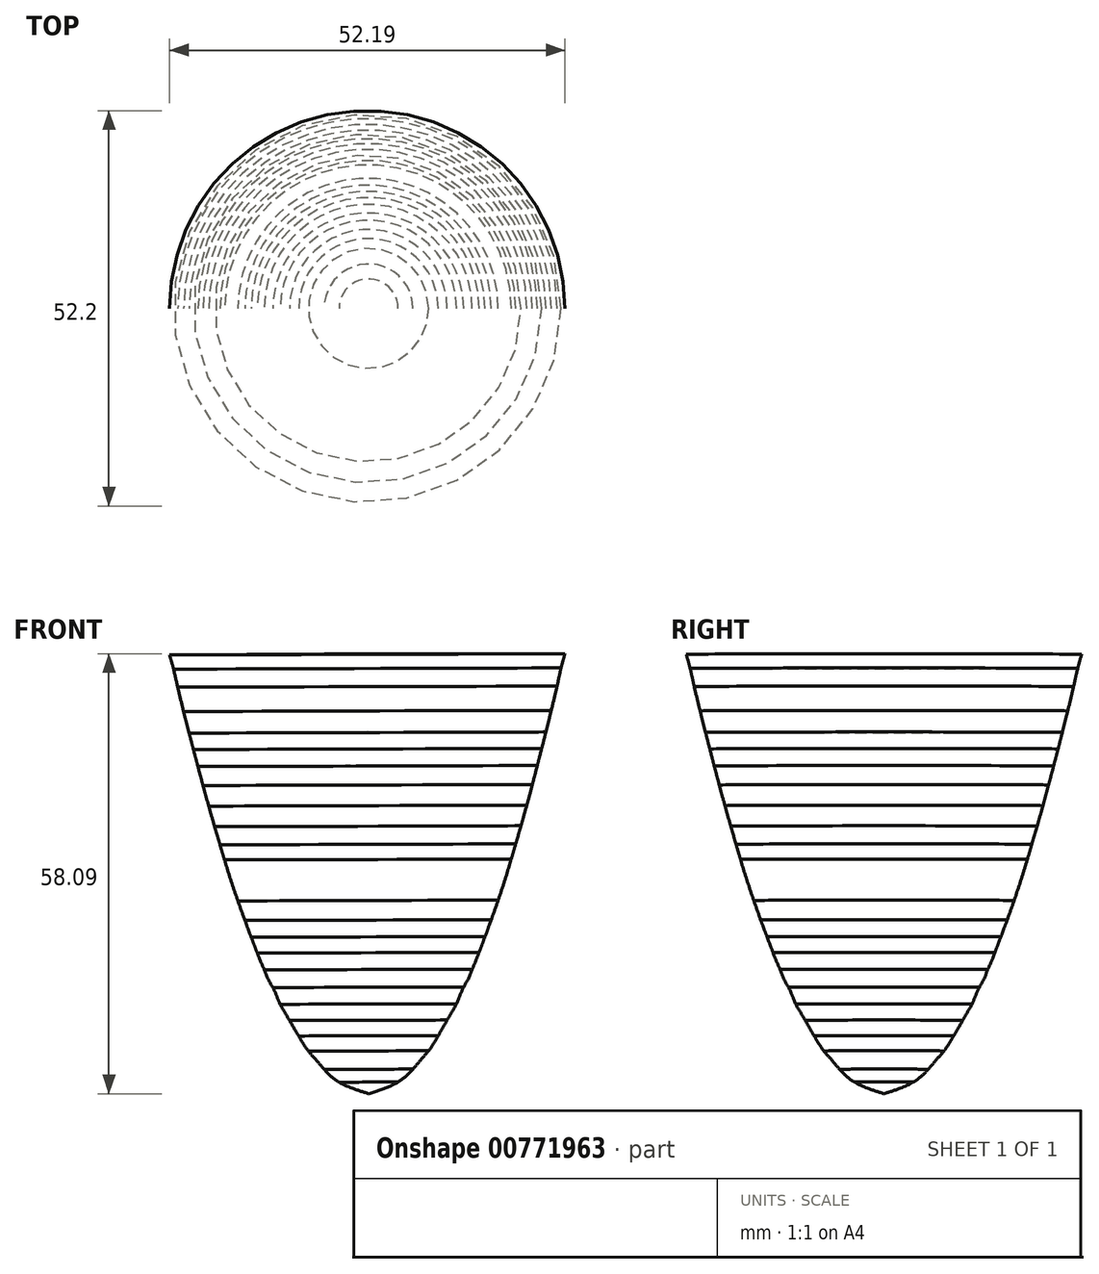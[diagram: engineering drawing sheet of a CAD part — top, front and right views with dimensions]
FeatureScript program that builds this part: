
annotation { "Feature Type Name" : "Feature", "Feature Type Description" : "" }
export const myFeature = defineFeature(function(context is Context, id is Id, definition is map)
    precondition{}
    {
        {
            var Q0;
            Q0=qCreatedBy(makeId("Front.planeOp"),FACE);
            var sketch = newSketch(context, id + "F0", { "sketchPlane" : qUnion([Q0])});
            skPoint(sketch, "E0", {"position": v(0.03, -0.02) * mm});
            skPoint(sketch, "E1", {"position": v(3.18, 1.13) * mm});
            skPoint(sketch, "E2", {"position": v(5.18, 2.5) * mm});
            skPoint(sketch, "E3", {"position": v(6.84, 4.37) * mm});
            skPoint(sketch, "E4", {"position": v(8.16, 5.94) * mm});
            skPoint(sketch, "E5", {"position": v(9.14, 7.52) * mm});
            skPoint(sketch, "E6", {"position": v(9.9, 8.84) * mm});
            skPoint(sketch, "E7", {"position": v(10.89, 10.54) * mm});
            skPoint(sketch, "E8", {"position": v(11.75, 12.1) * mm});
            skPoint(sketch, "E9", {"position": v(12.46, 13.83) * mm});
            skPoint(sketch, "E10", {"position": v(13.16, 15.1) * mm});
            skPoint(sketch, "E11", {"position": v(13.63, 16.27) * mm});
            skPoint(sketch, "E12", {"position": v(14.18, 17.52) * mm});
            skPoint(sketch, "E13", {"position": v(14.76, 19.04) * mm});
            skPoint(sketch, "E14", {"position": v(15.34, 20.55) * mm});
            skPoint(sketch, "E15", {"position": v(15.91, 22.07) * mm});
            skPoint(sketch, "E16", {"position": v(16.5, 23.66) * mm});
            skPoint(sketch, "E17", {"position": v(17, 25.39) * mm});
            skPoint(sketch, "E18", {"position": v(17.57, 26.83) * mm});
            skPoint(sketch, "E19", {"position": v(18.15, 28.78) * mm});
            skPoint(sketch, "E20", {"position": v(18.73, 30.87) * mm});
            skPoint(sketch, "E21", {"position": v(19.45, 32.97) * mm});
            skPoint(sketch, "E22", {"position": v(20.25, 35.58) * mm});
            skPoint(sketch, "E23", {"position": v(20.68, 37.74) * mm});
            skPoint(sketch, "E24", {"position": v(21.38, 39.85) * mm});
            skPoint(sketch, "E25", {"position": v(22, 42.1) * mm});
            skPoint(sketch, "E26", {"position": v(22.47, 44.2) * mm});
            skPoint(sketch, "E27", {"position": v(23.18, 47) * mm});
            skPoint(sketch, "E28", {"position": v(24.03, 50.12) * mm});
            skPoint(sketch, "E29", {"position": v(24.81, 53.4) * mm});
            skPoint(sketch, "E30", {"position": v(25.43, 56.2) * mm});
            skPoint(sketch, "E31", {"position": v(25.43, 58.07) * mm});
            skFitSpline(sketch, "E32", {"points": [v(0.03, -0.02) * mm, v(3.18, 1.13) * mm, v(5.18, 2.5) * mm, v(6.84, 4.37) * mm, v(8.16, 5.94) * mm, v(9.14, 7.52) * mm, v(9.9, 8.84) * mm, v(10.89, 10.54) * mm, v(11.75, 12.1) * mm, v(12.46, 13.83) * mm, v(13.16, 15.1) * mm, v(13.63, 16.27) * mm, v(14.18, 17.52) * mm, v(14.76, 19.04) * mm, v(15.34, 20.55) * mm, v(17.57, 26.83) * mm, v(19.45, 32.97) * mm, v(21.38, 39.85) * mm, v(24.81, 53.4) * mm, v(25.43, 56.2) * mm, v(25.95, 58.07) * mm], "startDerivative": vector(61.74, 19.66) * mm, "endDerivative": vector(13.33, 46) * mm});
            skLineSegment(sketch, "E33", {"start": v(25.95, 58.07) * mm, "end": v(-0.15, 58.07) * mm});
            skLineSegment(sketch, "E34", {"start": v(-0.15, 58.07) * mm, "end": v(0.03, -0.02) * mm});
            skLineSegment(sketch, "E35", {"start": v(19.45, 32.97) * mm, "end": v(-0.07, 32.97) * mm});
            skLineSegment(sketch, "E36", {"start": v(25.43, 56.2) * mm, "end": v(-0.14, 56.12) * mm});
            skLineSegment(sketch, "E37", {"start": v(23.97, 45.58) * mm, "end": v(-6.54, 45.48) * mm});
            skLineSegment(sketch, "E38", {"start": v(-4.68, 53.8) * mm, "end": v(34.04, 53.8) * mm});
            skLineSegment(sketch, "E39", {"start": v(-7.24, 50.6) * mm, "end": v(41.15, 50.6) * mm});
            skLineSegment(sketch, "E40", {"start": v(-7.24, 47.74) * mm, "end": v(38.8, 47.74) * mm});
            skLineSegment(sketch, "E41", {"start": v(-6.54, 43.31) * mm, "end": v(33.08, 43.31) * mm});
            skLineSegment(sketch, "E42", {"start": v(-6.61, 40.8) * mm, "end": v(35.36, 40.8) * mm});
            skLineSegment(sketch, "E43", {"start": v(-6.34, 38.08) * mm, "end": v(33.86, 38.08) * mm});
            skLineSegment(sketch, "E44", {"start": v(-4.24, 35.28) * mm, "end": v(35.36, 35.4) * mm});
            skLineSegment(sketch, "E45", {"start": v(-4.66, 30.97) * mm, "end": v(35.36, 30.97) * mm});
            skLineSegment(sketch, "E46", {"start": v(-4.61, 28.25) * mm, "end": v(32.86, 28.25) * mm});
            skLineSegment(sketch, "E47", {"start": v(-4.44, 25.54) * mm, "end": v(32.3, 25.54) * mm});
            skLineSegment(sketch, "E48", {"start": v(-4.61, 22.96) * mm, "end": v(29.5, 22.96) * mm});
            skLineSegment(sketch, "E49", {"start": v(-4.36, 20.74) * mm, "end": v(30.66, 20.74) * mm});
            skLineSegment(sketch, "E50", {"start": v(-4.32, 18.64) * mm, "end": v(26.14, 18.64) * mm});
            skLineSegment(sketch, "E51", {"start": v(-4.53, 16.42) * mm, "end": v(28.75, 16.42) * mm});
            skLineSegment(sketch, "E52", {"start": v(-4.37, 14.08) * mm, "end": v(25.46, 14.08) * mm});
            skLineSegment(sketch, "E53", {"start": v(-4.32, 11.86) * mm, "end": v(28.46, 11.86) * mm});
            skLineSegment(sketch, "E54", {"start": v(-4.25, 9.7) * mm, "end": v(25.28, 9.7) * mm});
            skLineSegment(sketch, "E55", {"start": v(-4.22, 7.66) * mm, "end": v(30.42, 7.66) * mm});
            skLineSegment(sketch, "E56", {"start": v(-4.18, 5.62) * mm, "end": v(24.54, 5.7) * mm});
            skLineSegment(sketch, "E57", {"start": v(-4.14, 3.23) * mm, "end": v(12.44, 3.23) * mm});
            skLineSegment(sketch, "E58", {"start": v(-4.34, 1.53) * mm, "end": v(8.85, 1.53) * mm});
            skSolve(sketch);
        }
        {
            var Q0;
            Q0=makeQuery(id+"F0.imprint","IMPRINT",FACE,{"disambiguationData":[TD([[makeQuery(id+"F0.imprint","IMPRINT",EDGE,{"derivedFrom":sQuery(id+"F0.wireOp",EDGE,"E32")}),1.0]])]});
            var Q1;
            Q1=sQuery(id+"F0.wireOp",EDGE,"E34");
            revolve(context, id + "F1", {"surfaceOperationType" : NewSurfaceOperationType.NEW, "entities" : qUnion([Q0]), "axis" : qUnion([Q1]), "revolveType" : RevolveType.FULL});
        }
        {
            var Q0;
            {var subQ0=sQuery(id+"F0.wireOp",EDGE,"E35");Q0=makeQuery(id+"F0.imprint","IMPRINT",FACE,{"disambiguationData":[TD([[makeQuery(id+"F0.imprint","IMPRINT",EDGE,{"derivedFrom":subQ0}),1.0]])]});}
            var Q1;
            Q1=sQuery(id+"F0.wireOp",EDGE,"E34");
            revolve(context, id + "F2", {"surfaceOperationType" : NewSurfaceOperationType.NEW, "entities" : qUnion([Q0]), "axis" : qUnion([Q1]), "revolveType" : RevolveType.FULL});
        }
        {
            var Q0;
            {var subQ0=sQuery(id+"F0.wireOp",EDGE,"E35");Q0=makeQuery(id+"F0.imprint","IMPRINT",FACE,{"disambiguationData":[TD([[makeQuery(id+"F0.imprint","IMPRINT",EDGE,{"derivedFrom":subQ0}),-1.0]])]});}
            var Q1;
            Q1=sQuery(id+"F0.wireOp",EDGE,"E34");
            revolve(context, id + "F3", {"surfaceOperationType" : NewSurfaceOperationType.NEW, "entities" : qUnion([Q0]), "axis" : qUnion([Q1]), "revolveType" : RevolveType.FULL});
        }
        {
            var Q0;
            {var subQ0=sQuery(id+"F0.wireOp",EDGE,"E36");Q0=makeQuery(id+"F0.imprint","IMPRINT",FACE,{"disambiguationData":[TD([[makeQuery(id+"F0.imprint","IMPRINT",EDGE,{"derivedFrom":subQ0}),1.0]])]});}
            var Q1;
            Q1=sQuery(id+"F0.wireOp",EDGE,"E34");
            revolve(context, id + "F4", {"surfaceOperationType" : NewSurfaceOperationType.NEW, "entities" : qUnion([Q0]), "axis" : qUnion([Q1]), "revolveType" : RevolveType.FULL});
        }
        {
            var Q0;
            {var subQ0=sQuery(id+"F0.wireOp",EDGE,"E33");Q0=makeQuery(id+"F0.imprint","IMPRINT",FACE,{"disambiguationData":[TD([[makeQuery(id+"F0.imprint","IMPRINT",EDGE,{"derivedFrom":subQ0}),1.0]])]});}
            var Q1;
            Q1=sQuery(id+"F0.wireOp",EDGE,"E34");
            revolve(context, id + "F5", {"surfaceOperationType" : NewSurfaceOperationType.NEW, "entities" : qUnion([Q0]), "axis" : qUnion([Q1]), "revolveType" : RevolveType.FULL});
        }
        {
            var Q0;
            {var subQ0=sQuery(id+"F0.wireOp",EDGE,"E39");var subQ1=sQuery(id+"F0.wireOp",EDGE,"E32");var subQ2=makeQuery(id+"F0.imprint","INTERSECT",VERTEX,{"derivedFrom":[subQ1,subQ0]});Q0=makeQuery(id+"F0.imprint","IMPRINT",FACE,{"disambiguationData":[TD([[makeQuery(id+"F0.imprint","IMPRINT",EDGE,{"disambiguationData":[TD([[subQ2,-1.0]])],"derivedFrom":subQ1}),1.0]])]});}
            var Q1;
            Q1=sQuery(id+"F0.wireOp",EDGE,"E34");
            revolve(context, id + "F6", {"surfaceOperationType" : NewSurfaceOperationType.NEW, "entities" : qUnion([Q0]), "axis" : qUnion([Q1]), "revolveType" : RevolveType.FULL});
        }
        {
            var Q0;
            {var subQ0=sQuery(id+"F0.wireOp",EDGE,"E40");var subQ1=sQuery(id+"F0.wireOp",EDGE,"E32");var subQ2=makeQuery(id+"F0.imprint","INTERSECT",VERTEX,{"derivedFrom":[subQ1,subQ0]});Q0=makeQuery(id+"F0.imprint","IMPRINT",FACE,{"disambiguationData":[TD([[makeQuery(id+"F0.imprint","IMPRINT",EDGE,{"disambiguationData":[TD([[subQ2,-1.0]])],"derivedFrom":subQ1}),1.0]])]});}
            var Q1;
            Q1=sQuery(id+"F0.wireOp",EDGE,"E34");
            revolve(context, id + "F7", {"surfaceOperationType" : NewSurfaceOperationType.NEW, "entities" : qUnion([Q0]), "axis" : qUnion([Q1]), "revolveType" : RevolveType.FULL});
        }
        {
            var Q0;
            {var subQ0=sQuery(id+"F0.wireOp",EDGE,"E37");var subQ1=sQuery(id+"F0.wireOp",EDGE,"E32");var subQ2=makeQuery(id+"F0.imprint","INTERSECT",VERTEX,{"derivedFrom":[subQ1,subQ0]});Q0=makeQuery(id+"F0.imprint","IMPRINT",FACE,{"disambiguationData":[TD([[makeQuery(id+"F0.imprint","IMPRINT",EDGE,{"disambiguationData":[TD([[subQ2,-1.0]])],"derivedFrom":subQ1}),1.0]])]});}
            var Q1;
            Q1=sQuery(id+"F0.wireOp",EDGE,"E34");
            revolve(context, id + "F8", {"surfaceOperationType" : NewSurfaceOperationType.NEW, "entities" : qUnion([Q0]), "axis" : qUnion([Q1]), "revolveType" : RevolveType.FULL});
        }
        {
            var Q0;
            {var subQ0=sQuery(id+"F0.wireOp",EDGE,"E41");var subQ1=sQuery(id+"F0.wireOp",EDGE,"E32");var subQ2=makeQuery(id+"F0.imprint","INTERSECT",VERTEX,{"derivedFrom":[subQ1,subQ0]});Q0=makeQuery(id+"F0.imprint","IMPRINT",FACE,{"disambiguationData":[TD([[makeQuery(id+"F0.imprint","IMPRINT",EDGE,{"disambiguationData":[TD([[subQ2,-1.0]])],"derivedFrom":subQ1}),1.0]])]});}
            var Q1;
            Q1=sQuery(id+"F0.wireOp",EDGE,"E34");
            revolve(context, id + "F9", {"surfaceOperationType" : NewSurfaceOperationType.NEW, "entities" : qUnion([Q0]), "axis" : qUnion([Q1]), "revolveType" : RevolveType.FULL});
        }
        {
            var Q0;
            {var subQ0=sQuery(id+"F0.wireOp",EDGE,"E42");var subQ1=sQuery(id+"F0.wireOp",EDGE,"E32");var subQ2=makeQuery(id+"F0.imprint","INTERSECT",VERTEX,{"derivedFrom":[subQ1,subQ0]});Q0=makeQuery(id+"F0.imprint","IMPRINT",FACE,{"disambiguationData":[TD([[makeQuery(id+"F0.imprint","IMPRINT",EDGE,{"disambiguationData":[TD([[subQ2,-1.0]])],"derivedFrom":subQ1}),1.0]])]});}
            var Q1;
            Q1=sQuery(id+"F0.wireOp",EDGE,"E34");
            revolve(context, id + "F10", {"surfaceOperationType" : NewSurfaceOperationType.NEW, "entities" : qUnion([Q0]), "axis" : qUnion([Q1]), "revolveType" : RevolveType.FULL});
        }
        {
            var Q0;
            {var subQ0=sQuery(id+"F0.wireOp",EDGE,"E43");var subQ1=sQuery(id+"F0.wireOp",EDGE,"E32");var subQ2=makeQuery(id+"F0.imprint","INTERSECT",VERTEX,{"derivedFrom":[subQ1,subQ0]});Q0=makeQuery(id+"F0.imprint","IMPRINT",FACE,{"disambiguationData":[TD([[makeQuery(id+"F0.imprint","IMPRINT",EDGE,{"disambiguationData":[TD([[subQ2,-1.0]])],"derivedFrom":subQ1}),1.0]])]});}
            var Q1;
            Q1=sQuery(id+"F0.wireOp",EDGE,"E34");
            revolve(context, id + "F11", {"surfaceOperationType" : NewSurfaceOperationType.NEW, "entities" : qUnion([Q0]), "axis" : qUnion([Q1]), "revolveType" : RevolveType.FULL});
        }
        {
            var Q0;
            {var subQ0=sQuery(id+"F0.wireOp",EDGE,"E44");var subQ1=sQuery(id+"F0.wireOp",EDGE,"E32");var subQ2=makeQuery(id+"F0.imprint","INTERSECT",VERTEX,{"derivedFrom":[subQ1,subQ0]});Q0=makeQuery(id+"F0.imprint","IMPRINT",FACE,{"disambiguationData":[TD([[makeQuery(id+"F0.imprint","IMPRINT",EDGE,{"disambiguationData":[TD([[subQ2,-1.0]])],"derivedFrom":subQ1}),1.0]])]});}
            var Q1;
            Q1=sQuery(id+"F0.wireOp",EDGE,"E34");
            revolve(context, id + "F12", {"surfaceOperationType" : NewSurfaceOperationType.NEW, "entities" : qUnion([Q0]), "axis" : qUnion([Q1]), "revolveType" : RevolveType.FULL});
        }
        {
            var Q0;
            {var subQ0=sQuery(id+"F0.wireOp",EDGE,"E46");var subQ1=sQuery(id+"F0.wireOp",EDGE,"E32");var subQ2=makeQuery(id+"F0.imprint","INTERSECT",VERTEX,{"derivedFrom":[subQ1,subQ0]});Q0=makeQuery(id+"F0.imprint","IMPRINT",FACE,{"disambiguationData":[TD([[makeQuery(id+"F0.imprint","IMPRINT",EDGE,{"disambiguationData":[TD([[subQ2,-1.0]])],"derivedFrom":subQ1}),1.0]])]});}
            var Q1;
            Q1=sQuery(id+"F0.wireOp",EDGE,"E34");
            revolve(context, id + "F13", {"surfaceOperationType" : NewSurfaceOperationType.NEW, "entities" : qUnion([Q0]), "axis" : qUnion([Q1]), "revolveType" : RevolveType.FULL});
        }
        {
            var Q0;
            {var subQ0=sQuery(id+"F0.wireOp",EDGE,"E47");var subQ1=sQuery(id+"F0.wireOp",EDGE,"E32");var subQ2=makeQuery(id+"F0.imprint","INTERSECT",VERTEX,{"derivedFrom":[subQ1,subQ0]});Q0=makeQuery(id+"F0.imprint","IMPRINT",FACE,{"disambiguationData":[TD([[makeQuery(id+"F0.imprint","IMPRINT",EDGE,{"disambiguationData":[TD([[subQ2,-1.0]])],"derivedFrom":subQ1}),1.0]])]});}
            var Q1;
            Q1=sQuery(id+"F0.wireOp",EDGE,"E34");
            revolve(context, id + "F14", {"operationType" : NewBodyOperationType.ADD, "surfaceOperationType" : NewSurfaceOperationType.NEW, "entities" : qUnion([Q0]), "axis" : qUnion([Q1]), "revolveType" : RevolveType.FULL});
        }
        {
            var Q0;
            {var subQ0=sQuery(id+"F0.wireOp",EDGE,"E48");var subQ1=sQuery(id+"F0.wireOp",EDGE,"E32");var subQ2=makeQuery(id+"F0.imprint","INTERSECT",VERTEX,{"derivedFrom":[subQ1,subQ0]});Q0=makeQuery(id+"F0.imprint","IMPRINT",FACE,{"disambiguationData":[TD([[makeQuery(id+"F0.imprint","IMPRINT",EDGE,{"disambiguationData":[TD([[subQ2,-1.0]])],"derivedFrom":subQ1}),1.0]])]});}
            var Q1;
            Q1=sQuery(id+"F0.wireOp",EDGE,"E34");
            revolve(context, id + "F15", {"surfaceOperationType" : NewSurfaceOperationType.NEW, "entities" : qUnion([Q0]), "axis" : qUnion([Q1]), "revolveType" : RevolveType.FULL});
        }
        {
            var Q0;
            {var subQ0=sQuery(id+"F0.wireOp",EDGE,"E49");var subQ1=sQuery(id+"F0.wireOp",EDGE,"E32");var subQ2=makeQuery(id+"F0.imprint","INTERSECT",VERTEX,{"derivedFrom":[subQ1,subQ0]});Q0=makeQuery(id+"F0.imprint","IMPRINT",FACE,{"disambiguationData":[TD([[makeQuery(id+"F0.imprint","IMPRINT",EDGE,{"disambiguationData":[TD([[subQ2,-1.0]])],"derivedFrom":subQ1}),1.0]])]});}
            var Q1;
            Q1=sQuery(id+"F0.wireOp",EDGE,"E34");
            revolve(context, id + "F16", {"surfaceOperationType" : NewSurfaceOperationType.NEW, "entities" : qUnion([Q0]), "axis" : qUnion([Q1]), "revolveType" : RevolveType.FULL});
        }
        {
            var Q0;
            {var subQ0=sQuery(id+"F0.wireOp",EDGE,"E50");var subQ1=sQuery(id+"F0.wireOp",EDGE,"E32");var subQ2=makeQuery(id+"F0.imprint","INTERSECT",VERTEX,{"derivedFrom":[subQ1,subQ0]});Q0=makeQuery(id+"F0.imprint","IMPRINT",FACE,{"disambiguationData":[TD([[makeQuery(id+"F0.imprint","IMPRINT",EDGE,{"disambiguationData":[TD([[subQ2,-1.0]])],"derivedFrom":subQ1}),1.0]])]});}
            var Q1;
            Q1=sQuery(id+"F0.wireOp",EDGE,"E34");
            revolve(context, id + "F17", {"surfaceOperationType" : NewSurfaceOperationType.NEW, "entities" : qUnion([Q0]), "axis" : qUnion([Q1]), "revolveType" : RevolveType.FULL});
        }
        {
            var Q0;
            {var subQ0=sQuery(id+"F0.wireOp",EDGE,"E51");var subQ1=sQuery(id+"F0.wireOp",EDGE,"E32");var subQ2=makeQuery(id+"F0.imprint","INTERSECT",VERTEX,{"derivedFrom":[subQ1,subQ0]});Q0=makeQuery(id+"F0.imprint","IMPRINT",FACE,{"disambiguationData":[TD([[makeQuery(id+"F0.imprint","IMPRINT",EDGE,{"disambiguationData":[TD([[subQ2,-1.0]])],"derivedFrom":subQ1}),1.0]])]});}
            var Q1;
            Q1=sQuery(id+"F0.wireOp",EDGE,"E34");
            revolve(context, id + "F18", {"surfaceOperationType" : NewSurfaceOperationType.NEW, "entities" : qUnion([Q0]), "axis" : qUnion([Q1]), "revolveType" : RevolveType.FULL});
        }
        {
            var Q0;
            {var subQ0=sQuery(id+"F0.wireOp",EDGE,"E52");var subQ1=sQuery(id+"F0.wireOp",EDGE,"E32");var subQ2=makeQuery(id+"F0.imprint","INTERSECT",VERTEX,{"derivedFrom":[subQ1,subQ0]});Q0=makeQuery(id+"F0.imprint","IMPRINT",FACE,{"disambiguationData":[TD([[makeQuery(id+"F0.imprint","IMPRINT",EDGE,{"disambiguationData":[TD([[subQ2,-1.0]])],"derivedFrom":subQ1}),1.0]])]});}
            var Q1;
            Q1=sQuery(id+"F0.wireOp",EDGE,"E34");
            revolve(context, id + "F19", {"surfaceOperationType" : NewSurfaceOperationType.NEW, "entities" : qUnion([Q0]), "axis" : qUnion([Q1]), "revolveType" : RevolveType.FULL});
        }
        {
            var Q0;
            {var subQ0=sQuery(id+"F0.wireOp",EDGE,"E53");var subQ1=sQuery(id+"F0.wireOp",EDGE,"E32");var subQ2=makeQuery(id+"F0.imprint","INTERSECT",VERTEX,{"derivedFrom":[subQ1,subQ0]});Q0=makeQuery(id+"F0.imprint","IMPRINT",FACE,{"disambiguationData":[TD([[makeQuery(id+"F0.imprint","IMPRINT",EDGE,{"disambiguationData":[TD([[subQ2,-1.0]])],"derivedFrom":subQ1}),1.0]])]});}
            var Q1;
            Q1=sQuery(id+"F0.wireOp",EDGE,"E34");
            revolve(context, id + "F20", {"surfaceOperationType" : NewSurfaceOperationType.NEW, "entities" : qUnion([Q0]), "axis" : qUnion([Q1]), "revolveType" : RevolveType.FULL});
        }
        {
            var Q0;
            {var subQ0=sQuery(id+"F0.wireOp",EDGE,"E54");var subQ1=sQuery(id+"F0.wireOp",EDGE,"E32");var subQ2=makeQuery(id+"F0.imprint","INTERSECT",VERTEX,{"derivedFrom":[subQ1,subQ0]});Q0=makeQuery(id+"F0.imprint","IMPRINT",FACE,{"disambiguationData":[TD([[makeQuery(id+"F0.imprint","IMPRINT",EDGE,{"disambiguationData":[TD([[subQ2,-1.0]])],"derivedFrom":subQ1}),1.0]])]});}
            var Q1;
            Q1=sQuery(id+"F0.wireOp",EDGE,"E34");
            revolve(context, id + "F21", {"surfaceOperationType" : NewSurfaceOperationType.NEW, "entities" : qUnion([Q0]), "axis" : qUnion([Q1]), "revolveType" : RevolveType.FULL});
        }
        {
            var Q0;
            {var subQ0=sQuery(id+"F0.wireOp",EDGE,"E55");var subQ1=sQuery(id+"F0.wireOp",EDGE,"E32");var subQ2=makeQuery(id+"F0.imprint","INTERSECT",VERTEX,{"derivedFrom":[subQ1,subQ0]});Q0=makeQuery(id+"F0.imprint","IMPRINT",FACE,{"disambiguationData":[TD([[makeQuery(id+"F0.imprint","IMPRINT",EDGE,{"disambiguationData":[TD([[subQ2,-1.0]])],"derivedFrom":subQ1}),1.0]])]});}
            var Q1;
            Q1=sQuery(id+"F0.wireOp",EDGE,"E34");
            revolve(context, id + "F22", {"surfaceOperationType" : NewSurfaceOperationType.NEW, "entities" : qUnion([Q0]), "axis" : qUnion([Q1]), "revolveType" : RevolveType.FULL});
        }
        {
            var Q0;
            {var subQ0=sQuery(id+"F0.wireOp",EDGE,"E56");var subQ1=sQuery(id+"F0.wireOp",EDGE,"E32");var subQ2=makeQuery(id+"F0.imprint","INTERSECT",VERTEX,{"derivedFrom":[subQ1,subQ0]});Q0=makeQuery(id+"F0.imprint","IMPRINT",FACE,{"disambiguationData":[TD([[makeQuery(id+"F0.imprint","IMPRINT",EDGE,{"disambiguationData":[TD([[subQ2,-1.0]])],"derivedFrom":subQ1}),1.0]])]});}
            var Q1;
            Q1=sQuery(id+"F0.wireOp",EDGE,"E34");
            revolve(context, id + "F23", {"surfaceOperationType" : NewSurfaceOperationType.NEW, "entities" : qUnion([Q0]), "axis" : qUnion([Q1]), "revolveType" : RevolveType.FULL});
        }
        {
            var Q0;
            {var subQ0=sQuery(id+"F0.wireOp",EDGE,"E57");var subQ1=sQuery(id+"F0.wireOp",EDGE,"E32");var subQ2=makeQuery(id+"F0.imprint","INTERSECT",VERTEX,{"derivedFrom":[subQ1,subQ0]});Q0=makeQuery(id+"F0.imprint","IMPRINT",FACE,{"disambiguationData":[TD([[makeQuery(id+"F0.imprint","IMPRINT",EDGE,{"disambiguationData":[TD([[subQ2,-1.0]])],"derivedFrom":subQ1}),1.0]])]});}
            var Q1;
            Q1=sQuery(id+"F0.wireOp",EDGE,"E34");
            revolve(context, id + "F24", {"surfaceOperationType" : NewSurfaceOperationType.NEW, "entities" : qUnion([Q0]), "axis" : qUnion([Q1]), "revolveType" : RevolveType.FULL});
        }
        {
            var Q0;
            {var subQ0=sQuery(id+"F0.wireOp",EDGE,"E58");var subQ1=sQuery(id+"F0.wireOp",EDGE,"E32");var subQ2=makeQuery(id+"F0.imprint","INTERSECT",VERTEX,{"derivedFrom":[subQ1,subQ0]});Q0=makeQuery(id+"F0.imprint","IMPRINT",FACE,{"disambiguationData":[TD([[makeQuery(id+"F0.imprint","IMPRINT",EDGE,{"disambiguationData":[TD([[subQ2,-1.0]])],"derivedFrom":subQ1}),1.0]])]});}
            var Q1;
            Q1=sQuery(id+"F0.wireOp",EDGE,"E34");
            revolve(context, id + "F25", {"surfaceOperationType" : NewSurfaceOperationType.NEW, "entities" : qUnion([Q0]), "axis" : qUnion([Q1]), "revolveType" : RevolveType.FULL});
        }
    });
